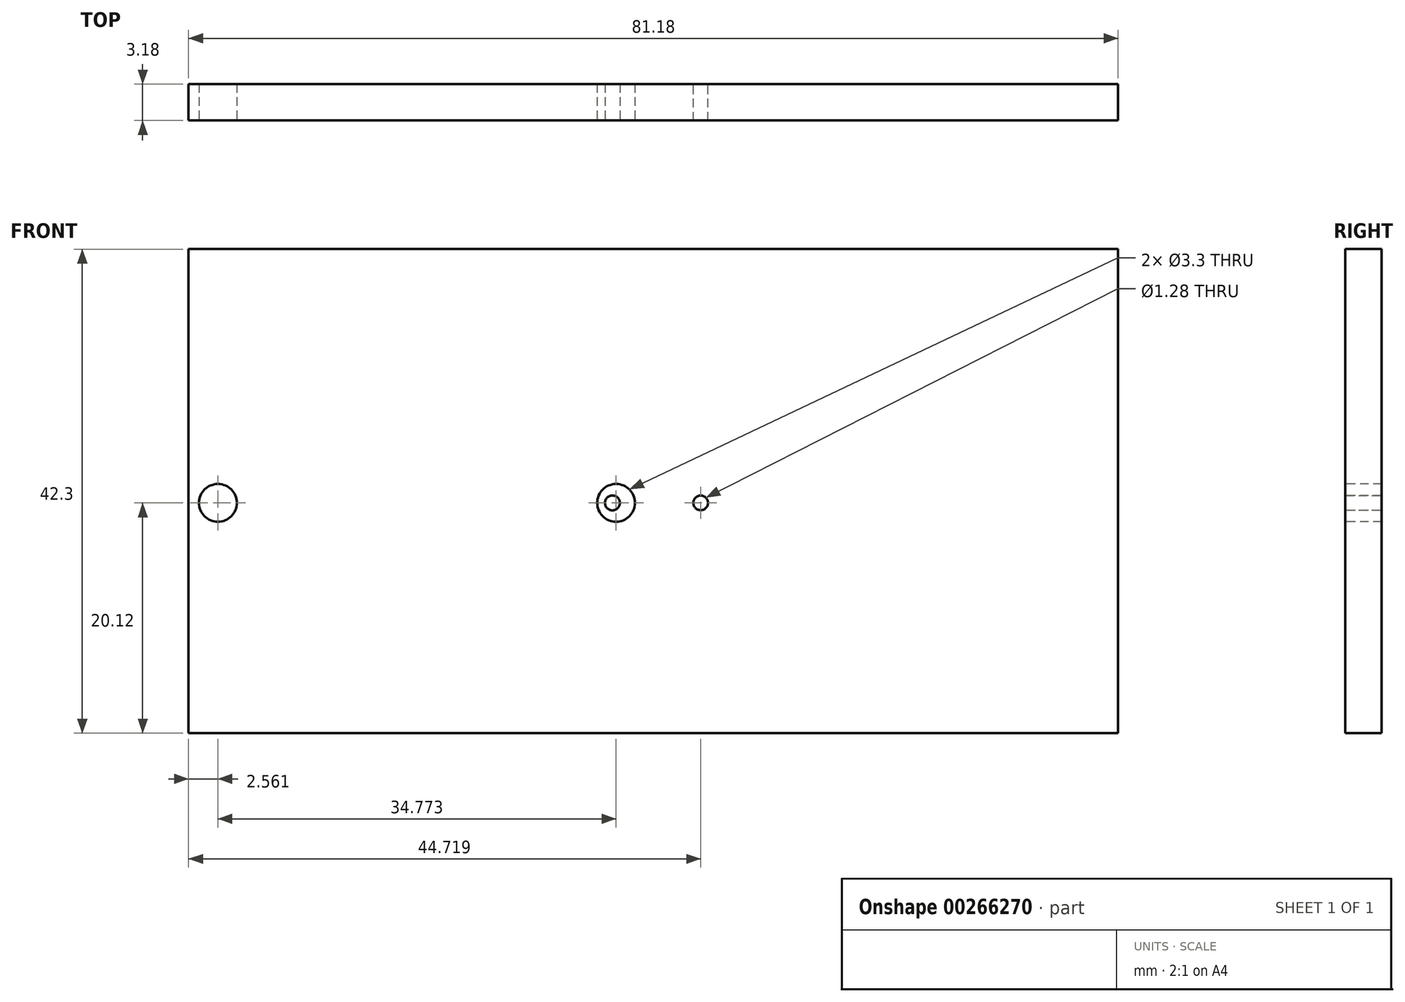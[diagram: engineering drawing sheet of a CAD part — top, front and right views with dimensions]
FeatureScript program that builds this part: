
annotation { "Feature Type Name" : "Feature", "Feature Type Description" : "" }
export const myFeature = defineFeature(function(context is Context, id is Id, definition is map)
    precondition{}
    {
        {
            var Q0;
            Q0=qCreatedBy(makeId("Front.planeOp"),FACE);
            var sketch = newSketch(context, id + "F0", { "sketchPlane" : qUnion([Q0])});
            skLineSegment(sketch, "E0.bottom", {"start": v(-40.11, 22.18) * mm, "end": v(41.07, 22.18) * mm});
            skLineSegment(sketch, "E0.top", {"start": v(-40.11, -20.12) * mm, "end": v(41.07, -20.12) * mm});
            skLineSegment(sketch, "E0.left", {"start": v(-40.11, 22.18) * mm, "end": v(-40.11, -20.12) * mm});
            skLineSegment(sketch, "E0.right", {"start": v(41.07, 22.18) * mm, "end": v(41.07, -20.12) * mm});
            skPoint(sketch, "E1", {"position": v(17.3, 0) * mm});
            skPoint(sketch, "E2", {"position": v(32.62, 0) * mm});
            skCircle(sketch, "E3", {"center": v(4.6, 0) * mm, "radius": 0.64 * mm});
            skSolve(sketch);
        }
        {
            var Q0;
            Q0 = qSketchRegion(id + "F0", true);
            extrude(context, id + "F1", {"entities" : qUnion([Q0]), "depth" : 3.17 * mm});
        }
        {
            var Q0;
            Q0=makeQuery(id+"F1.opExtrude","CAP_FACE",FACE,{"disambiguationData":[OSD([sQuery(id+"F0.wireOp",EDGE,"E0.bottom"),sQuery(id+"F0.wireOp",EDGE,"E0.top"),sQuery(id+"F0.wireOp",EDGE,"E0.left"),sQuery(id+"F0.wireOp",EDGE,"E0.right")])],"isStart":false});
            var sketch = newSketch(context, id + "F2", { "sketchPlane" : qUnion([Q0])});
            skCircle(sketch, "E4", {"center": v(-3.1, 0) * mm, "radius": 0.65 * mm});
            skCircle(sketch, "E5", {"center": v(-2.78, 0) * mm, "radius": 1.65 * mm});
            skCircle(sketch, "E6", {"center": v(-37.55, 0) * mm, "radius": 1.65 * mm});
            skSolve(sketch);
        }
        {
            var Q0;
            Q0 = qSketchRegion(id + "F2", true);
            extrude(context, id + "F3", {"entities" : qUnion([Q0]), "operationType" : NewBodyOperationType.REMOVE, "oppositeDirection" : true, "depth" : 12.7 * mm});
        }
        {
            var Q0;
            Q0 = qSketchRegion(id + "F0", true);
            extrude(context, id + "F4", {"entities" : qUnion([Q0]), "operationType" : NewBodyOperationType.REMOVE, "oppositeDirection" : true, "depth" : 25.4 * mm});
        }
    });
